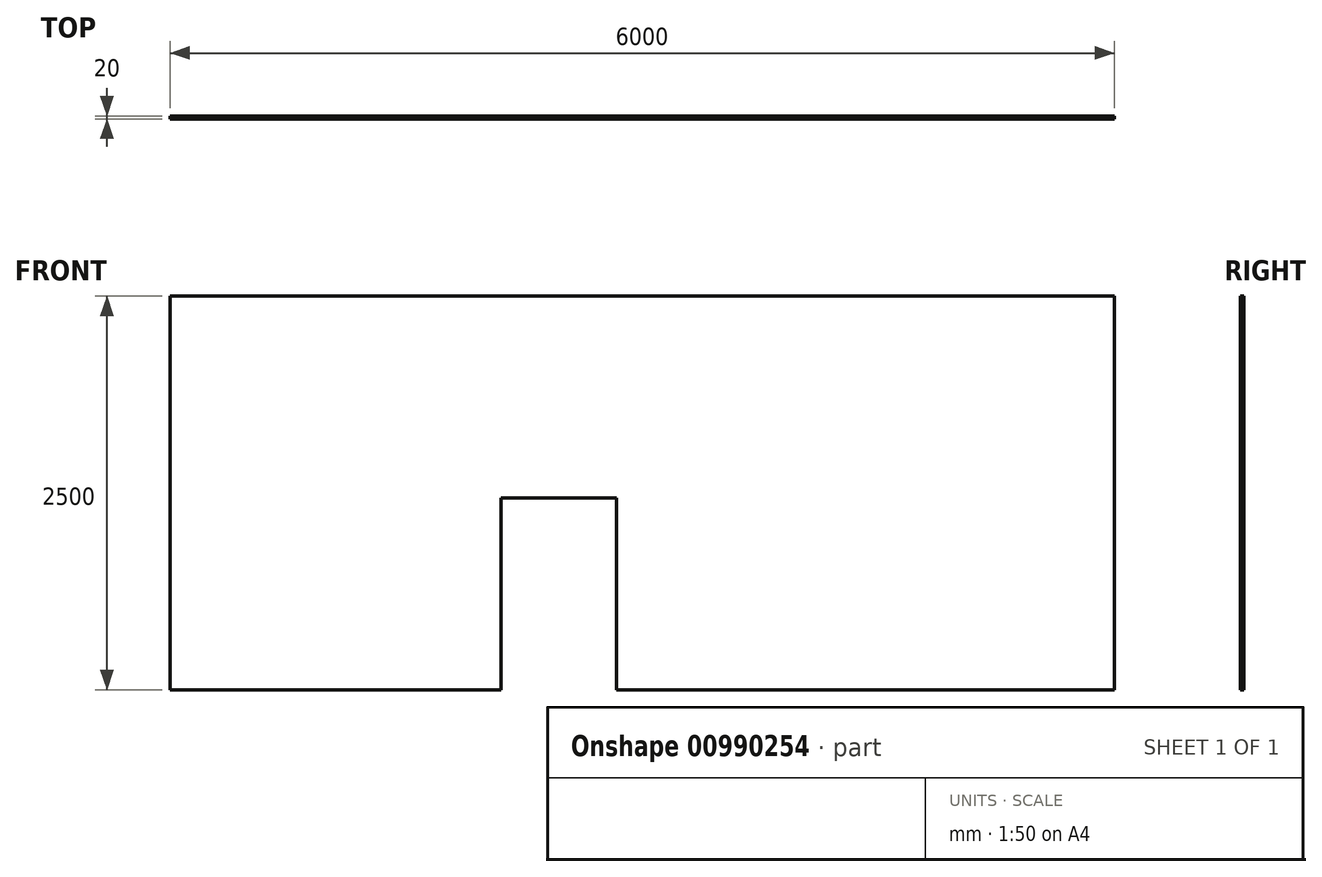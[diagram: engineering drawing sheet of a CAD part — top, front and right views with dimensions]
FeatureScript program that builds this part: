
annotation { "Feature Type Name" : "Feature", "Feature Type Description" : "" }
export const myFeature = defineFeature(function(context is Context, id is Id, definition is map)
    precondition{}
    {
        {
            var Q0;
            Q0=qCreatedBy(makeId("Front.planeOp"),FACE);
            var sketch = newSketch(context, id + "F0", { "sketchPlane" : qUnion([Q0])});
            skLineSegment(sketch, "E0.bottom", {"start": v(-3000.32, 1174.9) * mm, "end": v(2999.68, 1174.9) * mm});
            skLineSegment(sketch, "E0.top", {"start": v(-3000.32, -1325.1) * mm, "end": v(2999.68, -1325.1) * mm});
            skLineSegment(sketch, "E0.left", {"start": v(-3000.32, 1174.9) * mm, "end": v(-3000.32, -1325.1) * mm});
            skLineSegment(sketch, "E0.right", {"start": v(2999.68, 1174.9) * mm, "end": v(2999.68, -1325.1) * mm});
            skLineSegment(sketch, "E1.bottom", {"start": v(-898.27, -1325.1) * mm, "end": v(-165.13, -1325.1) * mm});
            skLineSegment(sketch, "E1.top", {"start": v(-898.27, -107.84) * mm, "end": v(-165.13, -107.84) * mm});
            skLineSegment(sketch, "E1.left", {"start": v(-898.27, -1325.1) * mm, "end": v(-898.27, -107.84) * mm});
            skLineSegment(sketch, "E1.right", {"start": v(-165.13, -1325.1) * mm, "end": v(-165.13, -107.84) * mm});
            skSolve(sketch);
        }
        {
            var Q0;
            Q0=makeQuery(id+"F0.imprint","IMPRINT",FACE,{"disambiguationData":[TD([[makeQuery(id+"F0.imprint","IMPRINT",EDGE,{"derivedFrom":sQuery(id+"F0.wireOp",EDGE,"E0.bottom")}),-1.0]])]});
            extrude(context, id + "F1", {"entities" : qUnion([Q0]), "depth" : 20 * mm, "offsetDistance" : 25 * mm});
        }
    });
